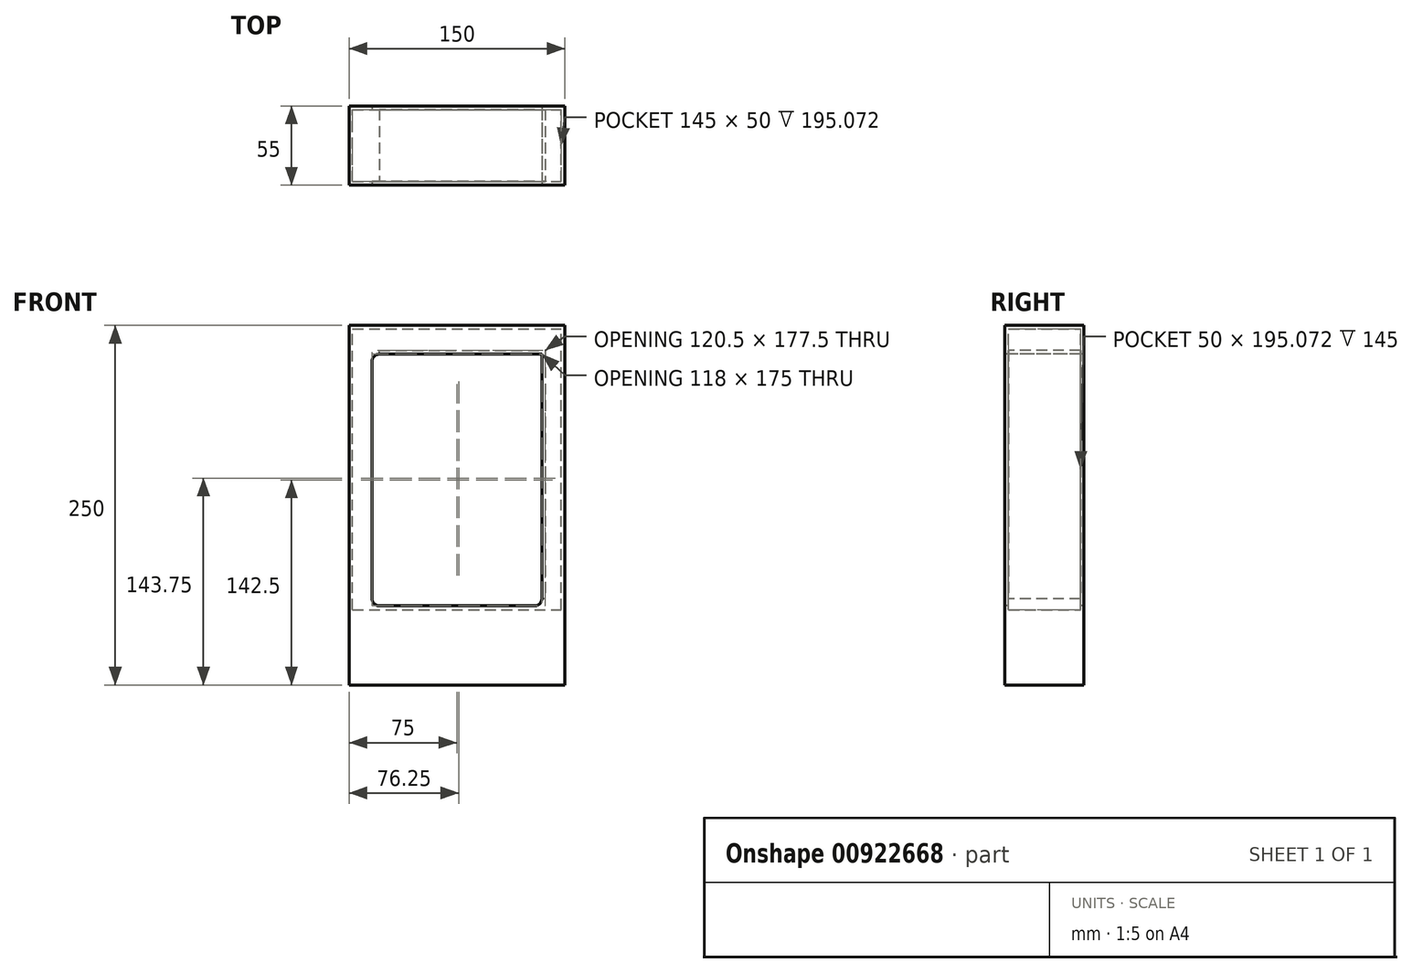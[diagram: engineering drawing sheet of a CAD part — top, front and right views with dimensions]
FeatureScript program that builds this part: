
annotation { "Feature Type Name" : "Feature", "Feature Type Description" : "" }
export const myFeature = defineFeature(function(context is Context, id is Id, definition is map)
    precondition{}
    {
        {
            var Q0;
            Q0=qCreatedBy(makeId("Front.planeOp"),FACE);
            var sketch = newSketch(context, id + "F0", { "sketchPlane" : qUnion([Q0])});
            skLineSegment(sketch, "E0.bottom", {"start": v(0, 0) * mm, "end": v(150, 0) * mm});
            skLineSegment(sketch, "E0.top", {"start": v(0, 250) * mm, "end": v(150, 250) * mm});
            skLineSegment(sketch, "E0.left", {"start": v(0, 0) * mm, "end": v(0, 250) * mm});
            skLineSegment(sketch, "E0.right", {"start": v(150, 0) * mm, "end": v(150, 250) * mm});
            skSolve(sketch);
        }
        {
            var Q0;
            Q0 = qSketchRegion(id + "F0", true);
            extrude(context, id + "F1", {"entities" : qUnion([Q0]), "depth" : 55 * mm, "offsetDistance" : 25 * mm});
        }
        {
            var Q0;
            Q0=makeQuery(id+"F1.opExtrude","CAP_FACE",FACE,{"disambiguationData":[OSD([sQuery(id+"F0.wireOp",EDGE,"E0.bottom"),sQuery(id+"F0.wireOp",EDGE,"E0.top"),sQuery(id+"F0.wireOp",EDGE,"E0.left"),sQuery(id+"F0.wireOp",EDGE,"E0.right")])],"isStart":false});
            var sketch = newSketch(context, id + "F2", { "sketchPlane" : qUnion([Q0])});
            skLineSegment(sketch, "E1", {"start": v(16, 230) * mm, "end": v(134, 230) * mm});
            skLineSegment(sketch, "E2", {"start": v(134, 230) * mm, "end": v(134, 55) * mm});
            skLineSegment(sketch, "E3.bottom", {"start": v(134, 55) * mm, "end": v(16, 55) * mm});
            skLineSegment(sketch, "E3.top", {"start": v(134, 230) * mm, "end": v(16, 230) * mm});
            skLineSegment(sketch, "E3.left", {"start": v(134, 55) * mm, "end": v(134, 230) * mm});
            skLineSegment(sketch, "E3.right", {"start": v(16, 55) * mm, "end": v(16, 230) * mm});
            skSolve(sketch);
        }
        {
            var Q0;
            Q0 = qSketchRegion(id + "F2", true);
            extrude(context, id + "F3", {"entities" : qUnion([Q0]), "operationType" : NewBodyOperationType.REMOVE, "endBound" : BoundingType.THROUGH_ALL, "oppositeDirection" : true, "depth" : 25 * mm, "offsetDistance" : 25 * mm});
        }
        {
            var Q0;
            Q0=makeQuery(id+"F3.boolean.opBoolean","COPY",EDGE,{"derivedFrom":makeQuery(id+"F3.opExtrude","SWEPT_EDGE",EDGE,{"disambiguationData":[OSD([sQuery(id+"F2.wireOp",EDGE,"E3.top"),sQuery(id+"F2.wireOp",EDGE,"E3.right")])]})});
            var Q1;
            Q1=makeQuery(id+"F3.boolean.opBoolean","COPY",EDGE,{"derivedFrom":makeQuery(id+"F3.opExtrude","SWEPT_EDGE",EDGE,{"disambiguationData":[OSD([sQuery(id+"F2.wireOp",EDGE,"E3.top"),sQuery(id+"F2.wireOp",EDGE,"E3.left")])]})});
            var Q2;
            Q2=makeQuery(id+"F3.boolean.opBoolean","COPY",EDGE,{"derivedFrom":makeQuery(id+"F3.opExtrude","SWEPT_EDGE",EDGE,{"disambiguationData":[OSD([sQuery(id+"F2.wireOp",EDGE,"E3.bottom"),sQuery(id+"F2.wireOp",EDGE,"E3.left")])]})});
            var Q3;
            Q3=makeQuery(id+"F3.boolean.opBoolean","COPY",EDGE,{"derivedFrom":makeQuery(id+"F3.opExtrude","SWEPT_EDGE",EDGE,{"disambiguationData":[OSD([sQuery(id+"F2.wireOp",EDGE,"E3.bottom"),sQuery(id+"F2.wireOp",EDGE,"E3.right")])]})});
            fillet(context, id + "F4", {"entities" : qUnion([Q0, Q1, Q2, Q3]), "radius" : 5 * mm, "tangentPropagation" : true, "allowEdgeOverflow" : false});
        }
        {
            var Q0;
            Q0=makeQuery(id+"F3.boolean.opBoolean","COPY",FACE,{"derivedFrom":makeQuery(id+"F3.opExtrude","SWEPT_FACE",FACE,{"disambiguationData":[OSD([sQuery(id+"F2.wireOp",EDGE,"E3.right")])]})});
            var Q1;
            Q1=makeQuery(id+"F4.opFillet","BLEND_FACE",FACE,{"disambiguationData":[OSD([sQuery(id+"F2.wireOp",EDGE,"E3.bottom"),sQuery(id+"F2.wireOp",EDGE,"E3.right")])]});
            var Q2;
            Q2=makeQuery(id+"F3.boolean.opBoolean","COPY",FACE,{"derivedFrom":makeQuery(id+"F3.opExtrude","SWEPT_FACE",FACE,{"disambiguationData":[OSD([sQuery(id+"F2.wireOp",EDGE,"E3.bottom")])]})});
            var Q3;
            Q3=makeQuery(id+"F4.opFillet","BLEND_FACE",FACE,{"disambiguationData":[OSD([sQuery(id+"F2.wireOp",EDGE,"E3.bottom"),sQuery(id+"F2.wireOp",EDGE,"E3.left")])]});
            var Q4;
            Q4=makeQuery(id+"F3.boolean.opBoolean","COPY",FACE,{"derivedFrom":makeQuery(id+"F3.opExtrude","SWEPT_FACE",FACE,{"disambiguationData":[OSD([sQuery(id+"F2.wireOp",EDGE,"E3.left")])]})});
            var Q5;
            Q5=makeQuery(id+"F4.opFillet","BLEND_FACE",FACE,{"disambiguationData":[OSD([sQuery(id+"F2.wireOp",EDGE,"E3.top"),sQuery(id+"F2.wireOp",EDGE,"E3.right")])]});
            var Q6;
            Q6=makeQuery(id+"F3.boolean.opBoolean","COPY",FACE,{"derivedFrom":makeQuery(id+"F3.opExtrude","SWEPT_FACE",FACE,{"disambiguationData":[OSD([sQuery(id+"F2.wireOp",EDGE,"E3.top")])]})});
            var Q7;
            Q7=makeQuery(id+"F4.opFillet","BLEND_FACE",FACE,{"disambiguationData":[OSD([sQuery(id+"F2.wireOp",EDGE,"E3.top"),sQuery(id+"F2.wireOp",EDGE,"E3.left")])]});
            shell(context, id + "F5", {"entities" : qUnion([Q0, Q1, Q2, Q3, Q4, Q5, Q6, Q7]), "thickness" : 2.5 * mm});
        }
        {
            var Q0;
            {var subQ0=sQuery(id+"F0.wireOp",EDGE,"E0.right");var subQ1=sQuery(id+"F0.wireOp",EDGE,"E0.left");var subQ2=sQuery(id+"F0.wireOp",EDGE,"E0.top");var subQ3=sQuery(id+"F0.wireOp",EDGE,"E0.bottom");Q0=makeQuery(id+"F5.opShell","OFFSET_FACE",FACE,{"disambiguationData":[OSD([subQ3,subQ2,subQ1,subQ0]),TDD([makeQuery(id+"F1.opExtrude","CAP_FACE",FACE,{"disambiguationData":[OSD([subQ3,subQ2,subQ1,subQ0])],"isStart":true})])]});}
            var sketch = newSketch(context, id + "F6", { "sketchPlane" : qUnion([Q0])});
            skLineSegment(sketch, "E4.bottom", {"start": v(2.5, 52.43) * mm, "end": v(147.5, 52.43) * mm});
            skLineSegment(sketch, "E4.top", {"start": v(2.5, 2.5) * mm, "end": v(147.5, 2.5) * mm});
            skLineSegment(sketch, "E4.left", {"start": v(2.5, 52.43) * mm, "end": v(2.5, 2.5) * mm});
            skLineSegment(sketch, "E4.right", {"start": v(147.5, 52.43) * mm, "end": v(147.5, 2.5) * mm});
            skSolve(sketch);
        }
        {
            var Q0;
            Q0 = qSketchRegion(id + "F6", true);
            extrude(context, id + "F7", {"entities" : qUnion([Q0]), "operationType" : NewBodyOperationType.ADD, "endBound" : BoundingType.UP_TO_NEXT, "depth" : 25 * mm, "offsetDistance" : 25 * mm});
        }
    });
